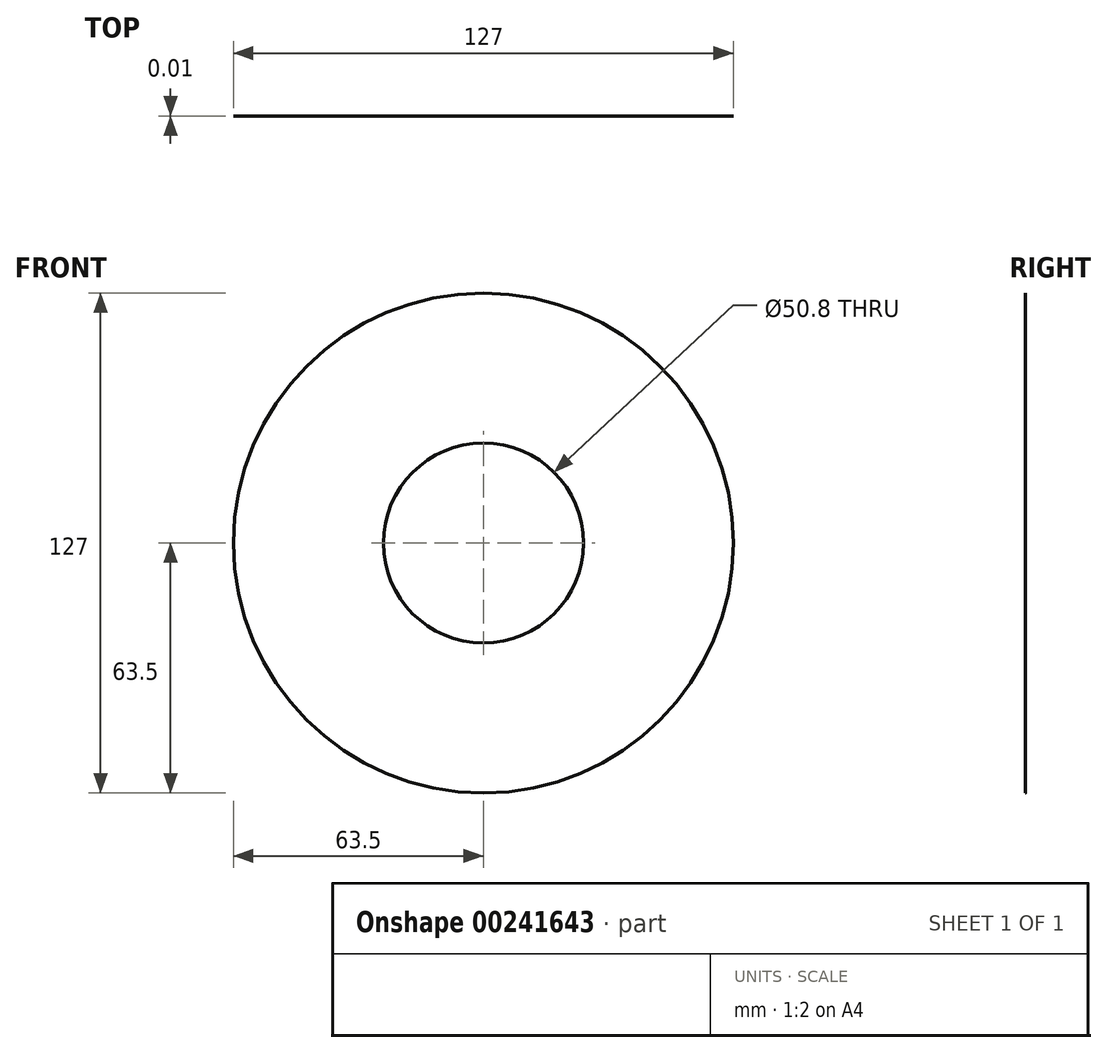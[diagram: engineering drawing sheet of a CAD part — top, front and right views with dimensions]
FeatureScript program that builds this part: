
annotation { "Feature Type Name" : "Feature", "Feature Type Description" : "" }
export const myFeature = defineFeature(function(context is Context, id is Id, definition is map)
    precondition{}
    {
        {
            var Q0;
            Q0=qCreatedBy(makeId("Front.planeOp"),FACE);
            var sketch = newSketch(context, id + "F0", { "sketchPlane" : qUnion([Q0])});
            skCircle(sketch, "E0", {"center": v(0, 0) * mm, "radius": 25.4 * mm});
            skCircle(sketch, "E1", {"center": v(0, 0) * mm, "radius": 63.5 * mm});
            skSolve(sketch);
        }
        {
            var Q0;
            Q0=makeQuery(id+"F0.imprint","IMPRINT",FACE,{"disambiguationData":[TD([[makeQuery(id+"F0.imprint","IMPRINT",EDGE,{"derivedFrom":sQuery(id+"F0.wireOp",EDGE,"E0")}),-1.0]])]});
            extrude(context, id + "F1", {"entities" : qUnion([Q0]), "depth" : 3 / 203.2 * mm});
        }
    });
